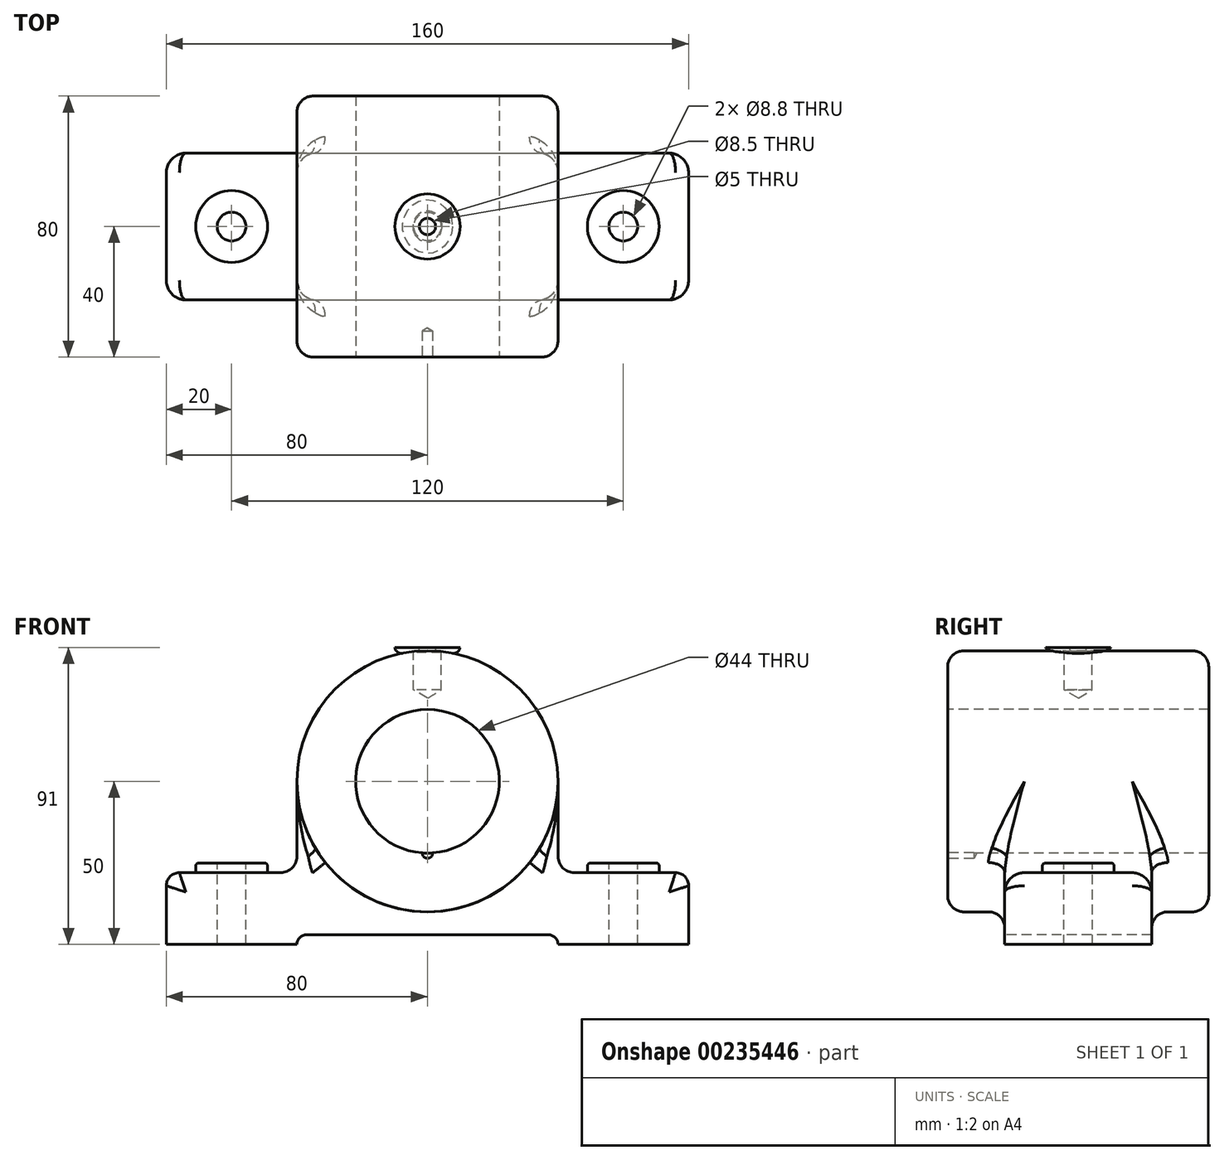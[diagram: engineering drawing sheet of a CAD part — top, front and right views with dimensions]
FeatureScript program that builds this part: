
annotation { "Feature Type Name" : "Feature", "Feature Type Description" : "" }
export const myFeature = defineFeature(function(context is Context, id is Id, definition is map)
    precondition{}
    {
        {
            var Q0;
            Q0=qCreatedBy(makeId("Front.planeOp"),FACE);
            var sketch = newSketch(context, id + "F0", { "sketchPlane" : qUnion([Q0])});
            skLineSegment(sketch, "E0", {"start": v(-80, 0) * mm, "end": v(-80, 22) * mm});
            skLineSegment(sketch, "E1", {"start": v(-80, 22) * mm, "end": v(-40, 22) * mm});
            skLineSegment(sketch, "E2", {"start": v(-40, 22) * mm, "end": v(-40, 50) * mm});
            skLineSegment(sketch, "E3", {"start": v(-40, 50) * mm, "end": v(0, 50) * mm});
            skLineSegment(sketch, "E4.MirrorCS", {"start": v(40, 50) * mm, "end": v(0, 50) * mm});
            skLineSegment(sketch, "E5.MirrorCS", {"start": v(80, 0) * mm, "end": v(80, 22) * mm});
            skLineSegment(sketch, "E6.MirrorCS", {"start": v(80, 22) * mm, "end": v(40, 22) * mm});
            skLineSegment(sketch, "E7.MirrorCS", {"start": v(40, 22) * mm, "end": v(40, 50) * mm});
            skLineSegment(sketch, "E8", {"start": v(-80, 0) * mm, "end": v(80, 0) * mm});
            skSolve(sketch);
        }
        {
            var Q0;
            Q0 = qSketchRegion(id + "F0", true);
            extrude(context, id + "F1", {"entities" : qUnion([Q0]), "depth" : 22.5 * mm, "hasSecondDirection" : true, "secondDirectionOppositeDirection" : true, "secondDirectionDepth" : 22.5 * mm});
        }
        {
            var Q0;
            Q0=qCreatedBy(makeId("Front.planeOp"),FACE);
            var sketch = newSketch(context, id + "F2", { "sketchPlane" : qUnion([Q0])});
            skCircle(sketch, "E9", {"center": v(0, 50) * mm, "radius": 40 * mm});
            skSolve(sketch);
        }
        {
            var Q0;
            Q0 = qSketchRegion(id + "F2", true);
            extrude(context, id + "F3", {"entities" : qUnion([Q0]), "operationType" : NewBodyOperationType.ADD, "depth" : 40 * mm, "hasSecondDirection" : true, "secondDirectionOppositeDirection" : true, "secondDirectionDepth" : 40 * mm});
        }
        {
            var Q0;
            Q0=makeQuery(id+"F3.opExtrude","CAP_FACE",FACE,{"disambiguationData":[OSD([sQuery(id+"F2.wireOp",EDGE,"E9")])],"isStart":false});
            var sketch = newSketch(context, id + "F4", { "sketchPlane" : qUnion([Q0])});
            skCircle(sketch, "E10", {"center": v(0, 50) * mm, "radius": 22 * mm});
            skSolve(sketch);
        }
        {
            var Q0;
            Q0 = qSketchRegion(id + "F4", true);
            extrude(context, id + "F5", {"entities" : qUnion([Q0]), "operationType" : NewBodyOperationType.REMOVE, "endBound" : BoundingType.THROUGH_ALL, "oppositeDirection" : true, "depth" : 25 * mm});
        }
        {
            var Q0;
            Q0=makeQuery(id+"F1.opExtrude","SWEPT_FACE",FACE,{"disambiguationData":[OSD([sQuery(id+"F0.wireOp",EDGE,"E1")])]});
            var sketch = newSketch(context, id + "F6", { "sketchPlane" : qUnion([Q0])});
            skCircle(sketch, "E11", {"center": v(-60, 0) * mm, "radius": 11 * mm});
            skCircle(sketch, "E12.MirrorC", {"center": v(60, 0) * mm, "radius": 11 * mm});
            skSolve(sketch);
        }
        {
            var Q0;
            Q0 = qSketchRegion(id + "F6", true);
            extrude(context, id + "F7", {"entities" : qUnion([Q0]), "operationType" : NewBodyOperationType.ADD, "depth" : 3 * mm});
        }
        {
            var Q0;
            Q0=qCreatedBy(makeId("Top.planeOp"),FACE);
            cPlane(context, id + "F8", {"entities" : qUnion([Q0]), "cplaneType" : CPlaneType.OFFSET, "offset" : 91 * mm, "width" : 150 * mm, "height" : 150 * mm});
        }
        {
            var Q0;
            Q0=qCreatedBy(id+"F8.planeOp",FACE);
            var sketch = newSketch(context, id + "F9", { "sketchPlane" : qUnion([Q0])});
            skCircle(sketch, "E13", {"center": v(0, 0) * mm, "radius": 10 * mm});
            skSolve(sketch);
        }
        {
            var Q0;
            Q0 = qSketchRegion(id + "F9", true);
            extrude(context, id + "F10", {"entities" : qUnion([Q0]), "endBound" : BoundingType.UP_TO_NEXT, "oppositeDirection" : true, "depth" : 25 * mm});
        }
        {
            var Q0;
            Q0=qCreatedBy(id+"F8.planeOp",FACE);
            var sketch = newSketch(context, id + "F11", { "sketchPlane" : qUnion([Q0])});
            skCircle(sketch, "E14", {"center": v(0, 0) * mm, "radius": 2.5 * mm});
            skSolve(sketch);
        }
        {
            var Q0;
            Q0 = qSketchRegion(id + "F11", true);
            extrude(context, id + "F12", {"entities" : qUnion([Q0]), "operationType" : NewBodyOperationType.REMOVE, "endBound" : BoundingType.UP_TO_NEXT, "oppositeDirection" : true, "depth" : 25 * mm});
        }
        {
            var Q0;
            Q0=qCreatedBy(id+"F8.planeOp",FACE);
            var sketch = newSketch(context, id + "F13", { "sketchPlane" : qUnion([Q0])});
            skPoint(sketch, "E15", {"position": v(0, 0) * mm});
            skSolve(sketch);
        }
        {
            var Q0;
            Q0=sQuery(id+"F13.wireOp",VERTEX,"E15");
            var Q1;
            Q1=makeQuery(id+"F1.opExtrude","SWEPT_BODY",BODY,{"disambiguationData":[OSD([sQuery(id+"F0.wireOp",EDGE,"E0"),sQuery(id+"F0.wireOp",EDGE,"E1"),sQuery(id+"F0.wireOp",EDGE,"E2"),sQuery(id+"F0.wireOp",EDGE,"E3"),sQuery(id+"F0.wireOp",EDGE,"E4.MirrorCS"),sQuery(id+"F0.wireOp",EDGE,"E5.MirrorCS"),sQuery(id+"F0.wireOp",EDGE,"E6.MirrorCS"),sQuery(id+"F0.wireOp",EDGE,"E7.MirrorCS"),sQuery(id+"F0.wireOp",EDGE,"E8")])]});
            hole(context, id + "F14", {"style" : HoleStyle.C_SINK, "endStyle" : HoleEndStyle.BLIND, "holeDiameter" : 8.5 * mm, "cSinkDiameter" : 11.5 * mm, "cSinkAngle" : 90 * degree, "holeDepth" : 13 * mm, "startFromSketch" : true, "locations" : qUnion([Q0]), "scope" : qUnion([Q1])});
        }
        {
            var Q0;
            Q0=makeQuery(id+"F7.opExtrude","CAP_FACE",FACE,{"disambiguationData":[OSD([sQuery(id+"F6.wireOp",EDGE,"E12.MirrorC")])],"isStart":false});
            var sketch = newSketch(context, id + "F15", { "sketchPlane" : qUnion([Q0])});
            skPoint(sketch, "E16", {"position": v(60, 0) * mm});
            skPoint(sketch, "E17.MirrorP", {"position": v(-60, 0) * mm});
            skSolve(sketch);
        }
        {
            var Q0;
            Q0=sQuery(id+"F15.wireOp",VERTEX,"E16");
            var Q1;
            Q1=sQuery(id+"F15.wireOp",VERTEX,"E17.MirrorP");
            var Q2;
            Q2=makeQuery(id+"F1.opExtrude","SWEPT_BODY",BODY,{"disambiguationData":[OSD([sQuery(id+"F0.wireOp",EDGE,"E0"),sQuery(id+"F0.wireOp",EDGE,"E1"),sQuery(id+"F0.wireOp",EDGE,"E2"),sQuery(id+"F0.wireOp",EDGE,"E3"),sQuery(id+"F0.wireOp",EDGE,"E4.MirrorCS"),sQuery(id+"F0.wireOp",EDGE,"E5.MirrorCS"),sQuery(id+"F0.wireOp",EDGE,"E6.MirrorCS"),sQuery(id+"F0.wireOp",EDGE,"E7.MirrorCS"),sQuery(id+"F0.wireOp",EDGE,"E8")])]});
            hole(context, id + "F16", {"style" : HoleStyle.SIMPLE, "endStyle" : HoleEndStyle.THROUGH, "standardTappedOrClearance" : lookupTablePath({ "standard" : "ISO", "fit" : "Normal", "engagement" : "75%", "pitch" : "1.25 mm", "size" : "M10", "type" : "Tapped" }), "standardBlindInLast" : lookupTablePath({ "fit" : "Standard", "standard" : "ISO", "engagement" : "75%", "pitch" : "1.25 mm", "size" : "M10", "type" : "Tapped" }), "holeDiameter" : 8.8 * mm, "locations" : qUnion([Q0, Q1]), "scope" : qUnion([Q2]), "isTappedThrough" : true, "majorDiameter" : 10 * mm, "showTappedDepth" : true});
        }
        {
            var Q0;
            Q0=qCreatedBy(makeId("Front.planeOp"),FACE);
            var sketch = newSketch(context, id + "F17", { "sketchPlane" : qUnion([Q0])});
            skLineSegment(sketch, "E18.bottom", {"start": v(-40, 3) * mm, "end": v(40, 3) * mm});
            skLineSegment(sketch, "E18.top", {"start": v(-40, -3) * mm, "end": v(40, -3) * mm});
            skLineSegment(sketch, "E18.left", {"start": v(-40, 3) * mm, "end": v(-40, -3) * mm});
            skLineSegment(sketch, "E18.right", {"start": v(40, 3) * mm, "end": v(40, -3) * mm});
            skPoint(sketch, "E18.middle", {"position": v(0, 0) * mm});
            skSolve(sketch);
        }
        {
            var Q0;
            Q0 = qSketchRegion(id + "F17", true);
            extrude(context, id + "F18", {"entities" : qUnion([Q0]), "operationType" : NewBodyOperationType.REMOVE, "endBound" : BoundingType.THROUGH_ALL, "oppositeDirection" : true, "depth" : 25 * mm, "hasSecondDirection" : true, "secondDirectionBound" : SecondDirectionBoundingType.THROUGH_ALL, "secondDirectionOppositeDirection" : false, "secondDirectionDepth" : 25 * mm});
        }
        {
            var Q0;
            Q0=makeQuery(id+"F18.boolean.opBoolean","COPY",EDGE,{"derivedFrom":makeQuery(id+"F18.opExtrude","SWEPT_EDGE",EDGE,{"disambiguationData":[OSD([sQuery(id+"F17.wireOp",EDGE,"E18.bottom"),sQuery(id+"F17.wireOp",EDGE,"E18.right")])]})});
            var Q1;
            Q1=makeQuery(id+"F18.boolean.opBoolean","COPY",EDGE,{"derivedFrom":makeQuery(id+"F18.opExtrude","SWEPT_EDGE",EDGE,{"disambiguationData":[OSD([sQuery(id+"F17.wireOp",EDGE,"E18.bottom"),sQuery(id+"F17.wireOp",EDGE,"E18.left")])]})});
            fillet(context, id + "F19", {"entities" : qUnion([Q0, Q1]), "radius" : 3 * mm, "tangentPropagation" : true, "allowEdgeOverflow" : false});
        }
        {
            var Q0;
            Q0=makeQuery(id+"F1.opExtrude","SWEPT_EDGE",EDGE,{"disambiguationData":[OSD([sQuery(id+"F0.wireOp",EDGE,"E5.MirrorCS"),sQuery(id+"F0.wireOp",EDGE,"E6.MirrorCS")])]});
            var Q1;
            Q1=makeQuery(id+"F1.opExtrude","SWEPT_EDGE",EDGE,{"disambiguationData":[OSD([sQuery(id+"F0.wireOp",EDGE,"E0"),sQuery(id+"F0.wireOp",EDGE,"E1")])]});
            fillet(context, id + "F20", {"entities" : qUnion([Q0, Q1]), "radius" : 4 * mm, "tangentPropagation" : true, "allowEdgeOverflow" : false});
        }
        {
            var Q0;
            Q0=makeQuery(id+"F1.opExtrude","SWEPT_EDGE",EDGE,{"disambiguationData":[OSD([sQuery(id+"F0.wireOp",EDGE,"E1"),sQuery(id+"F0.wireOp",EDGE,"E2")])]});
            var Q1;
            Q1=makeQuery(id+"F1.opExtrude","SWEPT_EDGE",EDGE,{"disambiguationData":[OSD([sQuery(id+"F0.wireOp",EDGE,"E6.MirrorCS"),sQuery(id+"F0.wireOp",EDGE,"E7.MirrorCS")])]});
            fillet(context, id + "F21", {"entities" : qUnion([Q0, Q1]), "radius" : 5 * mm, "tangentPropagation" : true, "allowEdgeOverflow" : false});
        }
        {
            var Q0;
            Q0=makeQuery(id+"F7.opExtrude","CAP_EDGE",EDGE,{"disambiguationData":[OSD([sQuery(id+"F6.wireOp",EDGE,"E11")])],"isStart":false});
            var Q1;
            Q1=makeQuery(id+"F7.opExtrude","CAP_EDGE",EDGE,{"disambiguationData":[OSD([sQuery(id+"F6.wireOp",EDGE,"E12.MirrorC")])],"isStart":false});
            fillet(context, id + "F22", {"entities" : qUnion([Q0, Q1]), "radius" : 1 * mm, "tangentPropagation" : true, "allowEdgeOverflow" : false});
        }
        {
            var Q0;
            Q0=makeQuery(id+"F7.opExtrude","CAP_EDGE",EDGE,{"disambiguationData":[OSD([sQuery(id+"F6.wireOp",EDGE,"E12.MirrorC")])],"isStart":true});
            var Q1;
            Q1=makeQuery(id+"F7.opExtrude","CAP_EDGE",EDGE,{"disambiguationData":[OSD([sQuery(id+"F6.wireOp",EDGE,"E11")])],"isStart":true});
            var Q2;
            Q2=makeQuery(id+"F10.opExtrude","CAP_EDGE",EDGE,{"disambiguationData":[OSD([sQuery(id+"F9.wireOp",EDGE,"E13")])],"isStart":false});
            fillet(context, id + "F23", {"entities" : qUnion([Q0, Q1, Q2]), "radius" : 2 * mm, "tangentPropagation" : true, "allowEdgeOverflow" : false});
        }
        {
            var Q0;
            Q0=makeQuery(id+"F1.opExtrude","CAP_EDGE",EDGE,{"disambiguationData":[OSD([sQuery(id+"F0.wireOp",EDGE,"E6.MirrorCS")])],"isStart":false});
            var Q1;
            Q1=makeQuery(id+"F1.opExtrude","CAP_EDGE",EDGE,{"disambiguationData":[OSD([sQuery(id+"F0.wireOp",EDGE,"E6.MirrorCS")])],"isStart":true});
            var Q2;
            Q2=makeQuery(id+"F1.opExtrude","CAP_EDGE",EDGE,{"disambiguationData":[OSD([sQuery(id+"F0.wireOp",EDGE,"E1")])],"isStart":false});
            var Q3;
            Q3=makeQuery(id+"F1.opExtrude","CAP_EDGE",EDGE,{"disambiguationData":[OSD([sQuery(id+"F0.wireOp",EDGE,"E1")])],"isStart":true});
            fillet(context, id + "F24", {"entities" : qUnion([Q0, Q1, Q2, Q3]), "radius" : 6 * mm, "tangentPropagation" : true, "allowEdgeOverflow" : false});
        }
        {
            var Q0;
            Q0=makeQuery(id+"F3.boolean.opBoolean","INTERSECT",EDGE,{"derivedFrom":[makeQuery(id+"F1.opExtrude","CAP_FACE",FACE,{"disambiguationData":[OSD([sQuery(id+"F0.wireOp",EDGE,"E0"),sQuery(id+"F0.wireOp",EDGE,"E1"),sQuery(id+"F0.wireOp",EDGE,"E2"),sQuery(id+"F0.wireOp",EDGE,"E3"),sQuery(id+"F0.wireOp",EDGE,"E4.MirrorCS"),sQuery(id+"F0.wireOp",EDGE,"E5.MirrorCS"),sQuery(id+"F0.wireOp",EDGE,"E6.MirrorCS"),sQuery(id+"F0.wireOp",EDGE,"E7.MirrorCS"),sQuery(id+"F0.wireOp",EDGE,"E8")])],"isStart":true}),makeQuery(id+"F3.opExtrude","SWEPT_FACE",FACE,{"disambiguationData":[OSD([sQuery(id+"F2.wireOp",EDGE,"E9")])]})]});
            var Q1;
            Q1=makeQuery(id+"F3.boolean.opBoolean","INTERSECT",EDGE,{"derivedFrom":[makeQuery(id+"F1.opExtrude","CAP_FACE",FACE,{"disambiguationData":[OSD([sQuery(id+"F0.wireOp",EDGE,"E0"),sQuery(id+"F0.wireOp",EDGE,"E1"),sQuery(id+"F0.wireOp",EDGE,"E2"),sQuery(id+"F0.wireOp",EDGE,"E3"),sQuery(id+"F0.wireOp",EDGE,"E4.MirrorCS"),sQuery(id+"F0.wireOp",EDGE,"E5.MirrorCS"),sQuery(id+"F0.wireOp",EDGE,"E6.MirrorCS"),sQuery(id+"F0.wireOp",EDGE,"E7.MirrorCS"),sQuery(id+"F0.wireOp",EDGE,"E8")])],"isStart":false}),makeQuery(id+"F3.opExtrude","SWEPT_FACE",FACE,{"disambiguationData":[OSD([sQuery(id+"F2.wireOp",EDGE,"E9")])]})]});
            var Q2;
            Q2=makeQuery(id+"F3.opExtrude","CAP_EDGE",EDGE,{"disambiguationData":[OSD([sQuery(id+"F2.wireOp",EDGE,"E9")])],"isStart":false});
            var Q3;
            Q3=makeQuery(id+"F3.opExtrude","CAP_EDGE",EDGE,{"disambiguationData":[OSD([sQuery(id+"F2.wireOp",EDGE,"E9")])],"isStart":true});
            fillet(context, id + "F25", {"entities" : qUnion([Q0, Q1, Q2, Q3]), "radius" : 5 * mm, "tangentPropagation" : true, "allowEdgeOverflow" : false});
        }
        {
            var Q0;
            Q0=makeQuery(id+"F3.opExtrude","CAP_FACE",FACE,{"disambiguationData":[OSD([sQuery(id+"F2.wireOp",EDGE,"E9")])],"isStart":false});
            var sketch = newSketch(context, id + "F26", { "sketchPlane" : qUnion([Q0])});
            skPoint(sketch, "E19", {"position": v(0, 28) * mm});
            skSolve(sketch);
        }
        {
            var Q0;
            Q0=sQuery(id+"F26.wireOp",VERTEX,"E19");
            var Q1;
            Q1=makeQuery(id+"F1.opExtrude","SWEPT_BODY",BODY,{"disambiguationData":[OSD([sQuery(id+"F0.wireOp",EDGE,"E0"),sQuery(id+"F0.wireOp",EDGE,"E1"),sQuery(id+"F0.wireOp",EDGE,"E2"),sQuery(id+"F0.wireOp",EDGE,"E3"),sQuery(id+"F0.wireOp",EDGE,"E4.MirrorCS"),sQuery(id+"F0.wireOp",EDGE,"E5.MirrorCS"),sQuery(id+"F0.wireOp",EDGE,"E6.MirrorCS"),sQuery(id+"F0.wireOp",EDGE,"E7.MirrorCS"),sQuery(id+"F0.wireOp",EDGE,"E8")])]});
            hole(context, id + "F27", {"style" : HoleStyle.SIMPLE, "endStyle" : HoleEndStyle.BLIND, "standardTappedOrClearance" : lookupTablePath({ "standard" : "ISO", "fit" : "Normal", "engagement" : "75%", "pitch" : "0.75 mm", "size" : "M4", "type" : "Tapped" }), "standardBlindInLast" : lookupTablePath({ "fit" : "Standard", "standard" : "ISO", "engagement" : "75%", "pitch" : "0.75 mm", "size" : "M4", "type" : "Tapped" }), "holeDiameter" : 3.2 * mm, "holeDepth" : 8 * mm, "locations" : qUnion([Q0]), "scope" : qUnion([Q1])});
        }
    });
